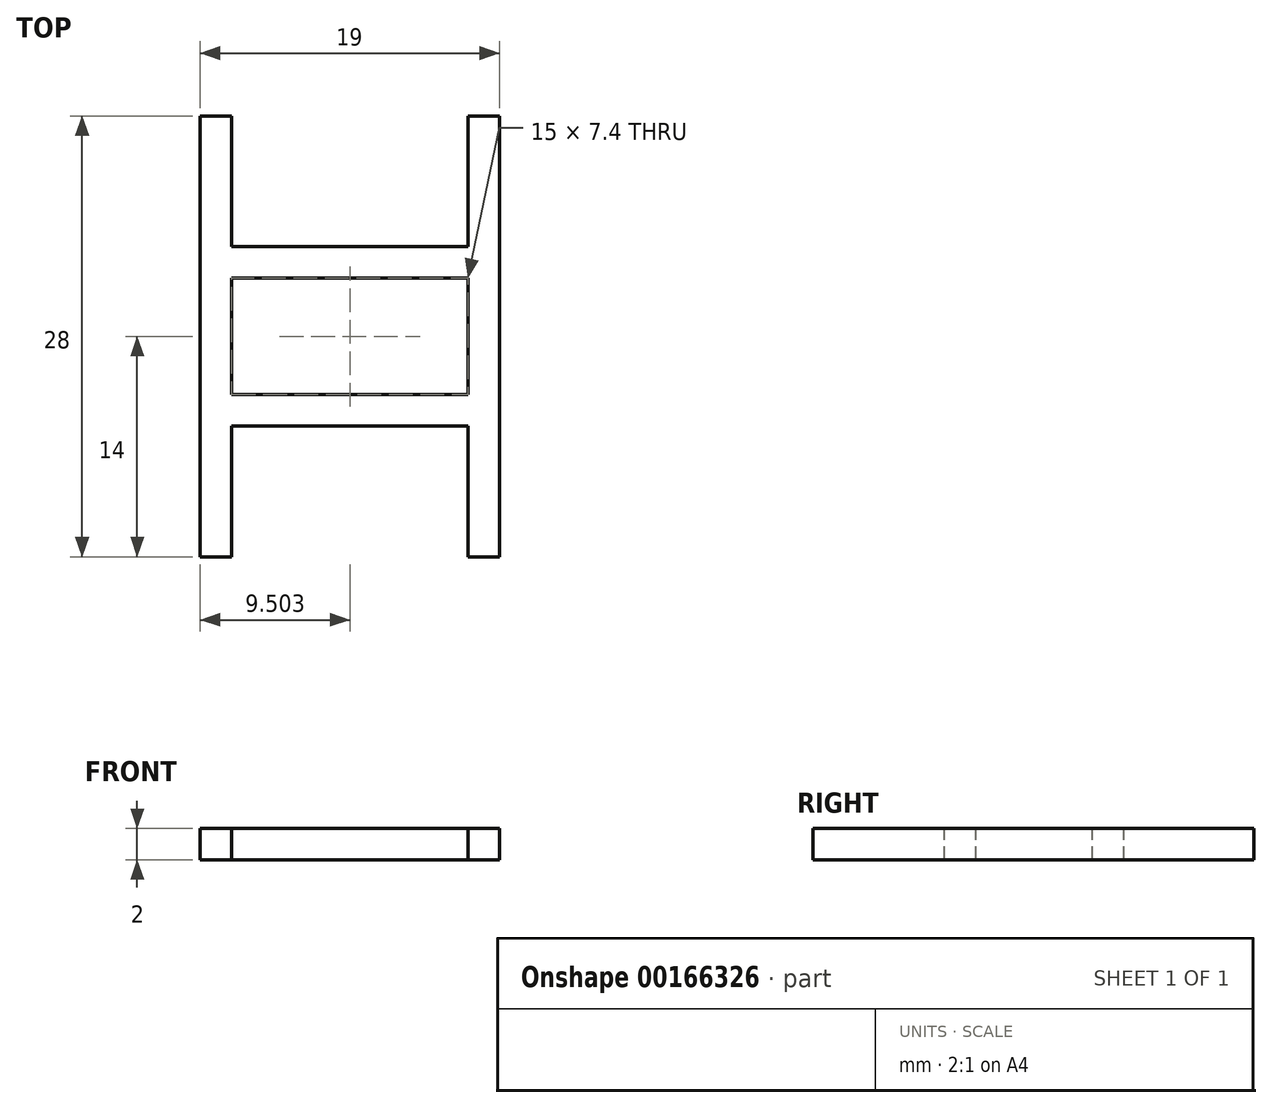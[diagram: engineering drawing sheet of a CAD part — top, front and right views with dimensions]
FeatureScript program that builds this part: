
annotation { "Feature Type Name" : "Feature", "Feature Type Description" : "" }
export const myFeature = defineFeature(function(context is Context, id is Id, definition is map)
    precondition{}
    {
        {
            var Q0;
            Q0=qCreatedBy(makeId("Front.planeOp"),FACE);
            var sketch = newSketch(context, id + "F0", { "sketchPlane" : qUnion([Q0])});
            skLineSegment(sketch, "E0.bottom", {"start": v(-30.22, 16.27) * mm, "end": v(-28.22, 16.27) * mm});
            skLineSegment(sketch, "E0.top", {"start": v(-30.22, 14.27) * mm, "end": v(-28.22, 14.27) * mm});
            skLineSegment(sketch, "E0.left", {"start": v(-30.22, 16.27) * mm, "end": v(-30.22, 14.27) * mm});
            skLineSegment(sketch, "E0.right", {"start": v(-28.22, 16.27) * mm, "end": v(-28.22, 14.27) * mm});
            skLineSegment(sketch, "E1.bottom", {"start": v(-13.22, 16.27) * mm, "end": v(-11.22, 16.27) * mm});
            skLineSegment(sketch, "E1.top", {"start": v(-13.22, 14.27) * mm, "end": v(-11.22, 14.27) * mm});
            skLineSegment(sketch, "E1.left", {"start": v(-13.22, 16.27) * mm, "end": v(-13.22, 14.27) * mm});
            skLineSegment(sketch, "E1.right", {"start": v(-11.22, 16.27) * mm, "end": v(-11.22, 14.27) * mm});
            skPoint(sketch, "E1.middle", {"position": v(-12.22, 15.27) * mm});
            skPoint(sketch, "E1.middle.positionSnap0", {"position": v(-28.22, 15.27) * mm});
            skPoint(sketch, "E1.centerSnap0", {"position": v(-28.22, 15.27) * mm});
            skSolve(sketch);
        }
        {
            var Q0;
            Q0=qSketchRegion(id+"F0",true);
            extrude(context, id + "F1", {"entities" : qUnion([Q0]), "depth" : 28 * mm});
        }
        {
            var Q0;
            Q0=makeQuery(id+"F1.opExtrude","SWEPT_FACE",FACE,{"disambiguationData":[OSD([sQuery(id+"F0.wireOp",EDGE,"E0.right")])]});
            var sketch = newSketch(context, id + "F2", { "sketchPlane" : qUnion([Q0])});
            skPoint(sketch, "E2.middle.positionSnap0", {"position": v(-28, 15.27) * mm});
            skPoint(sketch, "E2.centerSnap0", {"position": v(-28, 15.27) * mm});
            skLineSegment(sketch, "E3.bottom", {"start": v(-19.7, 16.27) * mm, "end": v(-17.7, 16.27) * mm});
            skLineSegment(sketch, "E3.top", {"start": v(-19.7, 14.27) * mm, "end": v(-17.7, 14.27) * mm});
            skLineSegment(sketch, "E3.left", {"start": v(-19.7, 16.27) * mm, "end": v(-19.7, 14.27) * mm});
            skLineSegment(sketch, "E3.right", {"start": v(-17.7, 16.27) * mm, "end": v(-17.7, 14.27) * mm});
            skPoint(sketch, "E3.middle", {"position": v(-18.7, 15.27) * mm});
            skLineSegment(sketch, "E4.bottom", {"start": v(-10.3, 16.27) * mm, "end": v(-8.3, 16.27) * mm});
            skLineSegment(sketch, "E4.top", {"start": v(-10.3, 14.27) * mm, "end": v(-8.3, 14.27) * mm});
            skLineSegment(sketch, "E4.left", {"start": v(-10.3, 16.27) * mm, "end": v(-10.3, 14.27) * mm});
            skLineSegment(sketch, "E4.right", {"start": v(-8.3, 16.27) * mm, "end": v(-8.3, 14.27) * mm});
            skPoint(sketch, "E4.middle", {"position": v(-9.3, 15.27) * mm});
            skPoint(sketch, "E4.middle.positionSnap0", {"position": v(0, 15.27) * mm});
            skPoint(sketch, "E4.centerSnap0", {"position": v(0, 15.27) * mm});
            skSolve(sketch);
        }
        {
            var Q0;
            Q0=makeQuery(id+"F2.imprint","IMPRINT",FACE,{"disambiguationData":[TD([[makeQuery(id+"F2.imprint","IMPRINT",EDGE,{"derivedFrom":sQuery(id+"F2.wireOp",EDGE,"E2.bottom")}),1.0]])]});
            var Q1;
            Q1=makeQuery(id+"F2.imprint","IMPRINT",FACE,{"disambiguationData":[TD([[makeQuery(id+"F2.imprint","IMPRINT",EDGE,{"derivedFrom":sQuery(id+"F2.wireOp",EDGE,"WnITUjJK-ytzY-J2tA-JWxi-fZO8ifMqTCVj.bottom")}),-1.0]])]});
            var Q2;
            Q2=makeQuery(id+"F2.imprint","IMPRINT",FACE,{"disambiguationData":[TD([[makeQuery(id+"F2.imprint","IMPRINT",EDGE,{"derivedFrom":sQuery(id+"F2.wireOp",EDGE,"Q3NBfuO8-VgWD-sKSG-JlKr-7RZjZvktvqla.bottom")}),-1.0]])]});
            var Q3;
            Q3=makeQuery(id+"F2.imprint","IMPRINT",FACE,{"disambiguationData":[TD([[makeQuery(id+"F2.imprint","IMPRINT",EDGE,{"derivedFrom":sQuery(id+"F2.wireOp",EDGE,"bFkEWhQn-0s3l-Hy1Z-3kmf-n2J4EL1Wdi8a.bottom")}),-1.0]])]});
            var Q4;
            Q4=makeQuery(id+"F2.imprint","IMPRINT",FACE,{"disambiguationData":[TD([[makeQuery(id+"F2.imprint","IMPRINT",EDGE,{"derivedFrom":sQuery(id+"F2.wireOp",EDGE,"E3.bottom")}),-1.0]])]});
            var Q5;
            Q5=makeQuery(id+"F2.imprint","IMPRINT",FACE,{"disambiguationData":[TD([[makeQuery(id+"F2.imprint","IMPRINT",EDGE,{"derivedFrom":sQuery(id+"F2.wireOp",EDGE,"E4.bottom")}),-1.0]])]});
            extrude(context, id + "F3", {"entities" : qUnion([Q0, Q1, Q2, Q3, Q4, Q5]), "operationType" : NewBodyOperationType.ADD, "depth" : 15 * mm});
        }
    });
